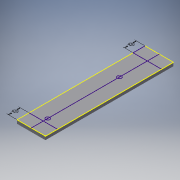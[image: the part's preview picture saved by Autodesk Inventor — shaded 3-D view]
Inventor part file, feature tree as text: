
AUTODESK INVENTOR PART (.ipt)
format: ipt  version: 2017 (Build 210142000, 142)  size: 107,520 bytes
history: native  units: in
note: dims shown in document units (in); Inventor stores cm internally (conversion verified against a paired STEP export)
features: sketch x5, other x3, reference x2, extrude x1
ambient origin geometry x8: Origin, YZ Plane, XZ Plane, XY Plane, X Axis, Y Axis, Z Axis, Center Point
bodies: Solid1 (feature_tree)
feature tree (11):
  extrude  "Extrusion1"  Depth=1.0in
  sketch  "Sketch2"  dims[d2=0.125in d3=0.0in]
  sketch  "Sketch3"  dims[d4=0.42in]
  sketch  "Sketch4"  dims[d5=0.42in]
  sketch  "Sketch5"
  sketch  "Sketch1"  dims[d0=4.5in d1=1.0in]
  reference  "Reference1"
  reference  "Reference2"
  other  "<userpath>\Documents\GitHub\RobotuxCAD\Team Robotux 15-16 Robot Cad Assets\Pickup 16.iam"
  other  "Pickup 16.iam"
  other  "tetrix_739089_2012:1"
